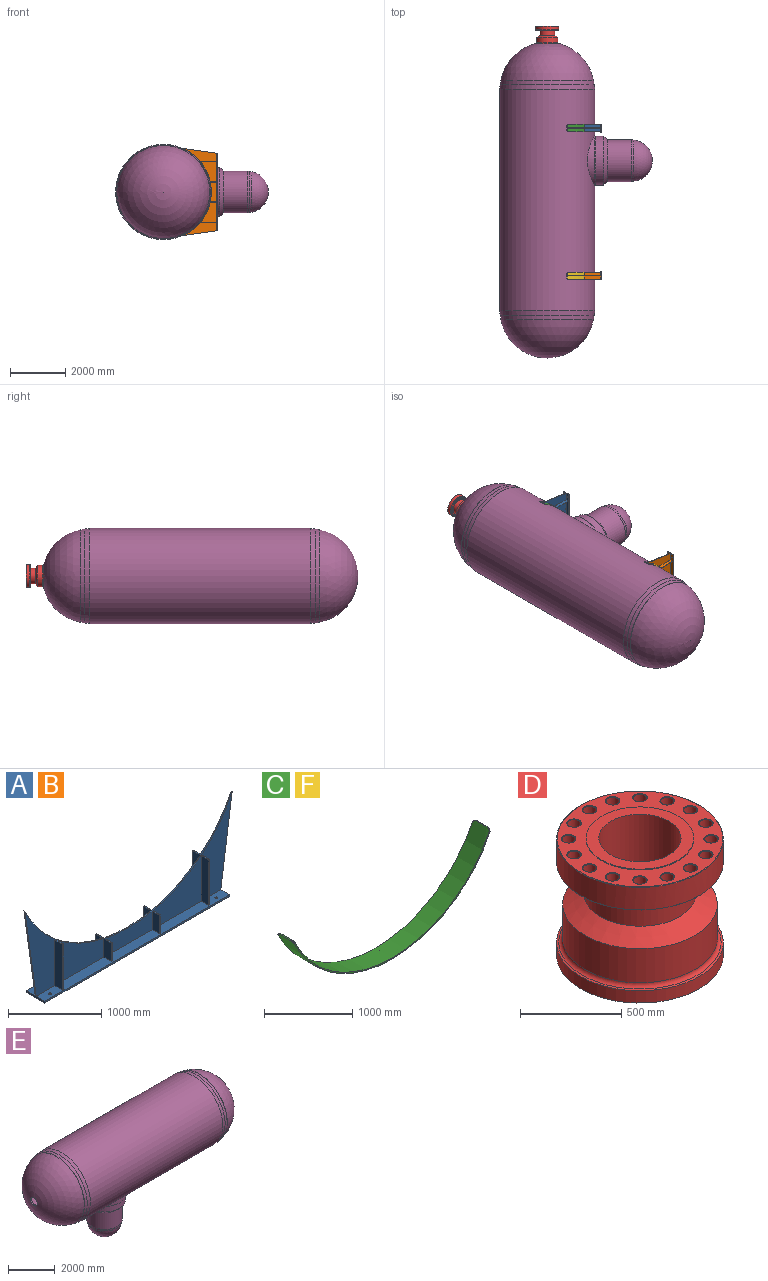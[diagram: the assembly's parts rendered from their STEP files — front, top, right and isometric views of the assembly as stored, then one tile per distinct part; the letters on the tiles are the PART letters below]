
ASSEMBLY  parts=6 mates=4
PART A: 56 faces, bbox 3143.1x280x1225.2 mm
  f0: plane 745x597.21mm, normal (0,1,0), area 280099.8mm2, adj f1,f12,f45,f46,f48
  f1: plane 2800x132mm, normal (0,0,1), area 360826.3mm2, adj f0,f2,f3,f4,f14,f15,f16,f17
  f2: plane 714x239.15mm, normal (0,1,0), area 153031mm2, adj f1,f12,f41,f44
  f3: plane 745x597.21mm, normal (0,1,0), area 280099.8mm2, adj f1,f12,f36,f40,f42
  f4: plane 1203.18x469.54mm, normal (0,1,0), area 287949.2mm2, adj f1,f10,f12,f49,f50
  f5: plane 1203.18x469.54mm, normal (0,-1,0), area 287949.2mm2, adj f6,f11,f12,f32,f34
  f6: plane 2800x132mm, normal (0,0,1), area 360826.3mm2, adj f5,f7,f8,f9,f13,f15,f17,f18
  f7: plane 745x597.21mm, normal (0,-1,0), area 280099.8mm2, adj f6,f12,f28,f29,f33
  f8: plane 714x239.15mm, normal (0,-1,0), area 153031mm2, adj f6,f12,f24,f30
  f9: plane 745x597.21mm, normal (0,-1,0), area 280099.8mm2, adj f6,f12,f20,f25,f26
  f10: plane 1203.18x171.54mm, normal (-0.99,0,-0.14), area 19445.5mm2, adj f4,f12,f13,f15
  f11: plane 1203.18x171.54mm, normal (0.99,0,-0.14), area 19445.5mm2, adj f5,f12,f14,f17
  f12: cylinder r=1734mm len=3143.08mm, axis (0,1,0), area 62949.1mm2, adj f0,f2,f3,f4,f5,f7,f8,f9
  f13: plane 1203.18x469.54mm, normal (0,-1,0), area 287949.2mm2, adj f6,f10,f12,f21,f22
  f14: plane 1203.18x469.54mm, normal (0,1,0), area 287949.2mm2, adj f1,f11,f12,f37,f38
  f15: plane 280x22mm, normal (-1,0,0), area 6160mm2, adj f1,f6,f10,f16,f18,f19
  f16: plane 2800x22mm, normal (0,1,0), area 61600mm2, adj f1,f15,f17,f19
  f17: plane 280x22mm, normal (1,0,0), area 6160mm2, adj f1,f6,f11,f16,f18,f19
  f18: plane 2800x22mm, normal (0,-1,0), area 61600mm2, adj f6,f15,f17,f19
  f19: plane 2800x280mm, normal (0,0,-1), area 781172.6mm2, adj f15,f16,f17,f18,f52,f53,f54,f55
  f20: plane 597.21x115mm, normal (1,0,0), area 68679.4mm2, adj f6,f9,f21,f23
  f21: plane 115x16mm, normal (0,0,1), area 1840mm2, adj f13,f20,f22,f23
  f22: plane 597.21x115mm, normal (-1,0,0), area 68679.4mm2, adj f6,f13,f21,f23
  f23: plane 597.21x16mm, normal (0,-1,0), area 9555.4mm2, adj f6,f20,f21,f22
  f24: plane 239.15x115mm, normal (1,0,0), area 27502mm2, adj f6,f8,f25,f27
  f25: plane 115x16mm, normal (0,0,1), area 1840mm2, adj f9,f24,f26,f27
  f26: plane 239.15x115mm, normal (-1,0,0), area 27502mm2, adj f6,f9,f25,f27
  f27: plane 239.15x16mm, normal (0,-1,0), area 3826.4mm2, adj f6,f24,f25,f26
  f28: plane 239.15x115mm, normal (1,0,0), area 27502mm2, adj f6,f7,f29,f31
  f29: plane 115x16mm, normal (0,0,1), area 1840mm2, adj f7,f28,f30,f31
  f30: plane 239.15x115mm, normal (-1,0,0), area 27502mm2, adj f6,f8,f29,f31
  f31: plane 239.15x16mm, normal (0,-1,0), area 3826.4mm2, adj f6,f28,f29,f30
  f32: plane 115x16mm, normal (0,0,1), area 1840mm2, adj f5,f33,f34,f35
  f33: plane 597.21x115mm, normal (-1,0,0), area 68679.4mm2, adj f6,f7,f32,f35
  f34: plane 597.21x115mm, normal (1,0,0), area 68679.4mm2, adj f5,f6,f32,f35
  f35: plane 597.21x16mm, normal (0,-1,0), area 9555.4mm2, adj f6,f32,f33,f34
  f36: plane 597.21x115mm, normal (-1,0,0), area 68679.4mm2, adj f1,f3,f37,f39
  f37: plane 115x16mm, normal (0,0,1), area 1840mm2, adj f14,f36,f38,f39
  f38: plane 597.21x115mm, normal (1,0,0), area 68679.4mm2, adj f1,f14,f37,f39
  f39: plane 597.21x16mm, normal (0,1,0), area 9555.4mm2, adj f1,f36,f37,f38
  f40: plane 239.15x115mm, normal (1,0,0), area 27502mm2, adj f1,f3,f42,f43
  f41: plane 239.15x115mm, normal (-1,0,0), area 27502mm2, adj f1,f2,f42,f43
  f42: plane 115x16mm, normal (0,0,1), area 1840mm2, adj f3,f40,f41,f43
  f43: plane 239.15x16mm, normal (0,1,0), area 3826.4mm2, adj f1,f40,f41,f42
  f44: plane 239.15x115mm, normal (1,0,0), area 27502mm2, adj f1,f2,f46,f47
  f45: plane 239.15x115mm, normal (-1,0,0), area 27502mm2, adj f0,f1,f46,f47
  f46: plane 115x16mm, normal (0,0,1), area 1840mm2, adj f0,f44,f45,f47
  f47: plane 239.15x16mm, normal (0,1,0), area 3826.4mm2, adj f1,f44,f45,f46
  f48: plane 597.21x115mm, normal (1,0,0), area 68679.4mm2, adj f0,f1,f50,f51
  f49: plane 597.21x115mm, normal (-1,0,0), area 68679.4mm2, adj f1,f4,f50,f51
  f50: plane 115x16mm, normal (0,0,1), area 1840mm2, adj f4,f48,f49,f51
  f51: plane 597.21x16mm, normal (0,1,0), area 9555.4mm2, adj f1,f48,f49,f50
  f52: cylinder r=15mm len=30mm, axis (0,0,-1), area 2073.5mm2, adj f6,f19
  f53: cylinder r=15mm len=30mm, axis (0,0,-1), area 2073.5mm2, adj f1,f19
  f54: cylinder r=15mm len=30mm, axis (0,0,-1), area 2073.5mm2, adj f6,f19
  f55: cylinder r=15mm len=30mm, axis (0,0,-1), area 2073.5mm2, adj f1,f19
PART B: same geometry as A
PART C: 11 faces, bbox 3155.6x270x1021.7 mm
  f0: cylinder r=1734mm len=3155.64mm, axis (0,1,0), area 1068188.4mm2, adj f2,f3,f4,f5,f6,f7,f8,f9
  f1: cylinder r=1718mm len=3126.52mm, axis (0,1,0), area 1058311.9mm2, adj f2,f3,f4,f5,f6,f7,f8,f9
  f2: plane 170x14.56mm, normal (0.41,0,0.91), area 2720mm2, adj f0,f1,f6,f8
  f3: plane 170x14.56mm, normal (-0.41,0,0.91), area 2720mm2, adj f0,f1,f7,f9
  f4: plane 3112.85x976.24mm, normal (0,-1,0), area 61536.3mm2, adj f0,f1,f8,f9
  f5: plane 3112.85x976.24mm, normal (0,1,0), area 61536.3mm2, adj f0,f1,f6,f7
  f6: cylinder r=50mm len=52.43mm, axis (0.91,0,-0.41), area 1256.8mm2, adj f0,f1,f2,f5
  f7: cylinder r=50mm len=52.43mm, axis (0.91,0,0.41), area 1256.8mm2, adj f0,f1,f3,f5
  f8: cylinder r=50mm len=52.43mm, axis (-0.91,0,0.41), area 1256.8mm2, adj f0,f1,f2,f4
  f9: cylinder r=50mm len=52.43mm, axis (-0.91,0,-0.41), area 1256.8mm2, adj f0,f1,f3,f4
  f10: cylinder r=3mm len=16mm, axis (0,0,-1), area 301.6mm2, adj f0,f1
PART D: 63 faces, bbox 882.1x882.1x707.7 mm
  f0: plane 820x820mm, normal (0,0,1), area 240041.4mm2, adj f1,f45,f46,f47,f48,f49,f50,f51
  f1: cylinder r=266.7mm len=533.4mm, axis (0,0,-1), area 8378.6mm2, adj f0,f2
  f2: plane 533.4x533.4mm, normal (0,0,1), area 93740.9mm2, adj f1,f3
  f3: cylinder r=203.2mm len=666.56mm, axis (0,0,-1), area 851029mm2, adj f2,f4
  f4: sphere r=1600mm, area 413508mm2, adj f3,f5
  f5: cylinder r=412.5mm len=825mm, axis (0,0,-1), area 192844.5mm2, adj f4,f6
  f6: sphere r=1672mm, area 29010.8mm2, adj f5,f62
  f7: cylinder r=382.5mm len=765mm, axis (0,0,-1), area 495707.3mm2, adj f8,f62
  f8: cone r=276.25mm half-angle=60deg, axis (0,0,-1), area 253903.6mm2, adj f7,f9
  f9: cylinder r=276.25mm len=552.5mm, axis (0,0,-1), area 334399.7mm2, adj f8,f10
  f10: plane 820x820mm, normal (0,0,-1), area 223751.7mm2, adj f9,f28,f29,f30,f31,f32,f33,f34
  f11: cylinder r=412.5mm len=825mm, axis (0,0,-1), area 352486.7mm2, adj f44,f45
  f12: cylinder r=33.35mm len=136mm, axis (0,0,1), area 28498mm2, adj f30,f52
  f13: cylinder r=33.35mm len=136mm, axis (0,0,1), area 28498mm2, adj f29,f51
  f14: cylinder r=33.35mm len=136mm, axis (0,0,1), area 28498mm2, adj f28,f50
  f15: cylinder r=33.35mm len=136mm, axis (0,0,1), area 28498mm2, adj f43,f49
  f16: cylinder r=33.35mm len=136mm, axis (0,0,1), area 28498mm2, adj f42,f48
  f17: cylinder r=33.35mm len=136mm, axis (0,0,1), area 28498mm2, adj f41,f47
  f18: cylinder r=33.35mm len=136mm, axis (0,0,1), area 28498mm2, adj f40,f46
  f19: cylinder r=33.35mm len=136mm, axis (0,0,1), area 28498mm2, adj f39,f61
  f20: cylinder r=33.35mm len=136mm, axis (0,0,1), area 28498mm2, adj f38,f60
  f21: cylinder r=33.35mm len=136mm, axis (0,0,1), area 28498mm2, adj f37,f59
  f22: cylinder r=33.35mm len=136mm, axis (0,0,1), area 28498mm2, adj f36,f58
  f23: cylinder r=33.35mm len=136mm, axis (0,0,1), area 28498mm2, adj f35,f57
  f24: cylinder r=33.35mm len=136mm, axis (0,0,1), area 28498mm2, adj f34,f56
  f25: cylinder r=33.35mm len=136mm, axis (0,0,1), area 28498mm2, adj f33,f55
  f26: cylinder r=33.35mm len=136mm, axis (0,0,1), area 28498mm2, adj f32,f54
  f27: cylinder r=33.35mm len=136mm, axis (0,0,1), area 28498mm2, adj f31,f53
  f28: cone r=35.85mm half-angle=45deg, axis (0,0,-1), area 768.6mm2, adj f10,f14
  f29: cone r=35.85mm half-angle=45deg, axis (0,0,-1), area 768.6mm2, adj f10,f13
  f30: cone r=35.85mm half-angle=45deg, axis (0,0,-1), area 768.6mm2, adj f10,f12
  f31: cone r=35.85mm half-angle=45deg, axis (0,0,-1), area 768.6mm2, adj f10,f27
  f32: cone r=35.85mm half-angle=45deg, axis (0,0,-1), area 768.6mm2, adj f10,f26
  f33: cone r=35.85mm half-angle=45deg, axis (0,0,-1), area 768.6mm2, adj f10,f25
  f34: cone r=35.85mm half-angle=45deg, axis (0,0,-1), area 768.6mm2, adj f10,f24
  f35: cone r=35.85mm half-angle=45deg, axis (0,0,-1), area 768.6mm2, adj f10,f23
  f36: cone r=35.85mm half-angle=45deg, axis (0,0,-1), area 768.6mm2, adj f10,f22
  f37: cone r=35.85mm half-angle=45deg, axis (0,0,-1), area 768.6mm2, adj f10,f21
  f38: cone r=35.85mm half-angle=45deg, axis (0,0,-1), area 768.6mm2, adj f10,f20
  f39: cone r=35.85mm half-angle=45deg, axis (0,0,-1), area 768.6mm2, adj f10,f19
  f40: cone r=35.85mm half-angle=45deg, axis (0,0,-1), area 768.6mm2, adj f10,f18
  f41: cone r=35.85mm half-angle=45deg, axis (0,0,-1), area 768.6mm2, adj f10,f17
  f42: cone r=35.85mm half-angle=45deg, axis (0,0,-1), area 768.6mm2, adj f10,f16
  f43: cone r=35.85mm half-angle=45deg, axis (0,0,-1), area 768.6mm2, adj f10,f15
  f44: cone r=410mm half-angle=45deg, axis (0,0,1), area 9135.7mm2, adj f10,f11
  f45: cone r=412.5mm half-angle=45deg, axis (0,0,-1), area 9135.7mm2, adj f0,f11
  f46: cone r=35.85mm half-angle=45deg, axis (0,0,1), area 768.6mm2, adj f0,f18
  f47: cone r=35.85mm half-angle=45deg, axis (0,0,1), area 768.6mm2, adj f0,f17
  f48: cone r=35.85mm half-angle=45deg, axis (0,0,1), area 768.6mm2, adj f0,f16
  f49: cone r=35.85mm half-angle=45deg, axis (0,0,1), area 768.6mm2, adj f0,f15
  f50: cone r=35.85mm half-angle=45deg, axis (0,0,1), area 768.6mm2, adj f0,f14
  f51: cone r=35.85mm half-angle=45deg, axis (0,0,1), area 768.6mm2, adj f0,f13
  f52: cone r=35.85mm half-angle=45deg, axis (0,0,1), area 768.6mm2, adj f0,f12
  f53: cone r=35.85mm half-angle=45deg, axis (0,0,1), area 768.6mm2, adj f0,f27
  f54: cone r=35.85mm half-angle=45deg, axis (0,0,1), area 768.6mm2, adj f0,f26
  f55: cone r=35.85mm half-angle=45deg, axis (0,0,1), area 768.6mm2, adj f0,f25
  f56: cone r=35.85mm half-angle=45deg, axis (0,0,1), area 768.6mm2, adj f0,f24
  f57: cone r=35.85mm half-angle=45deg, axis (0,0,1), area 768.6mm2, adj f0,f23
  f58: cone r=35.85mm half-angle=45deg, axis (0,0,1), area 768.6mm2, adj f0,f22
  f59: cone r=35.85mm half-angle=45deg, axis (0,0,1), area 768.6mm2, adj f0,f21
  f60: cone r=35.85mm half-angle=45deg, axis (0,0,1), area 768.6mm2, adj f0,f20
  f61: cone r=35.85mm half-angle=45deg, axis (0,0,1), area 768.6mm2, adj f0,f19
  f62: torus R=407.5mm, axis (0,0,-1), area 81212.1mm2, adj f6,f7
PART E: 27 faces, bbox 11392.5x3436x5511.1 mm
  f0: cylinder r=1718mm len=8000mm, axis (-1,0,0), area 83503033.5mm2, adj f5,f6,f15,f16,f21,f22,f23
  f1: sphere r=1703mm, area 14836242.4mm2, adj f2
  f2: plane 3347.57x3347.57mm, normal (1,0,0), area 4732.1mm2, adj f1,f3
  f3: cone r=1675.15mm half-angle=8deg, axis (-1,0,0), area 103724.3mm2, adj f2,f4
  f4: sphere r=1703mm, area 1514576.9mm2, adj f3,f5
  f5: cone r=1718mm half-angle=8deg, axis (-1,0,0), area 1780928.1mm2, adj f0,f4
  f6: cone r=1718mm half-angle=8deg, axis (1,0,0), area 1780928.1mm2, adj f0,f7
  f7: sphere r=1703mm, area 1514576.9mm2, adj f6,f8
  f8: cone r=1675.15mm half-angle=8deg, axis (1,0,0), area 103724.3mm2, adj f7,f9
  f9: plane 3347.57x3347.57mm, normal (-1,0,0), area 4732.1mm2, adj f8,f10
  f10: sphere r=1703mm, area 14706060.3mm2, adj f9,f11
  f11: cylinder r=203.2mm len=406.4mm, axis (1,0,0), area 92616.5mm2, adj f10,f12
  f12: sphere r=1631mm, area 13340919.7mm2, adj f11,f13
  f13: cylinder r=1600mm len=8631.61mm, axis (-1,0,0), area 85193322.5mm2, adj f12,f14,f26
  f14: sphere r=1631mm, area 13471144.1mm2, adj f13
  f15: plane 1866.54x878.15mm, normal (0,0,-1), area 82627.4mm2, adj f0,f21,f23
  f16: cylinder r=935mm len=1866.54mm, axis (0,0,1), area 394791.3mm2, adj f0,f22
  f17: cone r=880.24mm half-angle=45deg, axis (0,0,1), area 916631.1mm2, adj f18,f24
  f18: cylinder r=754mm len=1508mm, axis (0,0,1), area 4140594mm2, adj f17,f19
  f19: cone r=754mm half-angle=8.7deg, axis (0,0,1), area 380413.3mm2, adj f18,f20
  f20: sphere r=746mm, area 3121627.9mm2, adj f19
  f21: cylinder r=935mm len=1866.54mm, axis (0,0,1), area 394791.3mm2, adj f0,f15
  f22: plane 1866.54x878.15mm, normal (0,0,-1), area 82627.4mm2, adj f0,f16,f23
  f23: torus R=905.24mm, axis (0,0,1), area 218206.7mm2, adj f0,f15,f22,f24
  f24: cylinder r=880.24mm len=1760.49mm, axis (0,0,1), area 1685523mm2, adj f17,f23
  f25: sphere r=713mm, area 2587004mm2, adj f26
  f26: cylinder r=700mm len=1743.85mm, axis (0,0,1), area 7310156.8mm2, adj f13,f25
PART F: same geometry as C
PLACE A rot(axis=(0,-1,0),90deg) t=(-744.75,370.15,642.95)mm
PLACE B rot(axis=(0,-1,0),90deg) t=(-744.75,-4956.85,642.95)mm
PLACE C rot(axis=(0,-1,0),90deg) t=(-744.75,378.15,642.95)mm
PLACE D rot(axis=(0,0.71,0.71),180deg) t=(-744.75,3354.35,642.95)mm
PLACE E rot(axis=(0.58,-0.58,-0.58),120deg) t=(-744.75,1693.37,642.95)mm
PLACE F rot(axis=(0,-1,0),90deg) t=(-744.75,-4956.85,642.95)mm
MATE cylindrical C.f0 <-> A.f12  axis (0,1,0) through (-744.75,370.15,642.95)mm
MATE cylindrical F.f0 <-> E.f0  axis (0,1,0) through (-744.75,-4964.85,642.95)mm
MATE fastened E.f11 <-> D.f1  axis (0,-1,0) through (-744.75,3387.78,642.95)mm
MATE cylindrical C.f1 <-> E.f0  axis (0,1,0) through (-744.75,370.15,642.95)mm
